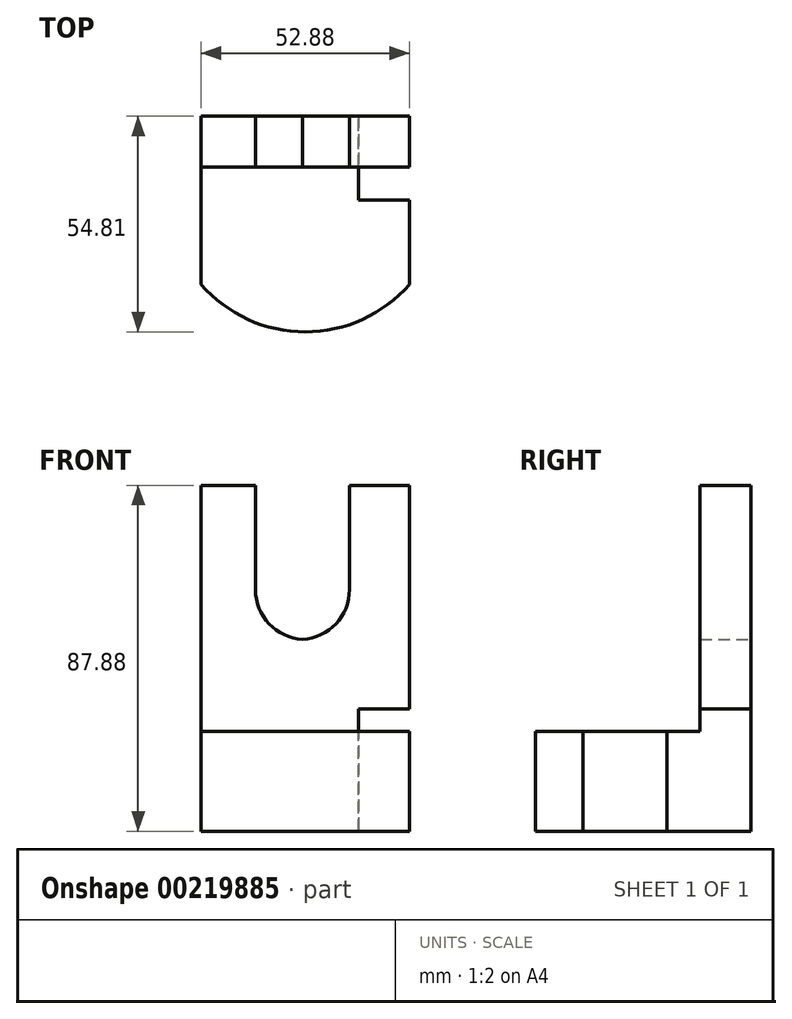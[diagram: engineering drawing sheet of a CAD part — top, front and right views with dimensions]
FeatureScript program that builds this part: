
annotation { "Feature Type Name" : "Feature", "Feature Type Description" : "" }
export const myFeature = defineFeature(function(context is Context, id is Id, definition is map)
    precondition{}
    {
        {
            var Q0;
            Q0=qCreatedBy(makeId("Top.planeOp"),FACE);
            var sketch = newSketch(context, id + "F0", { "sketchPlane" : qUnion([Q0])});
            skLineSegment(sketch, "E0", {"start": v(-27.7, 17.9) * mm, "end": v(25.17, 17.9) * mm});
            skLineSegment(sketch, "E1", {"start": v(25.17, 17.9) * mm, "end": v(25.17, -11.9) * mm});
            skLineSegment(sketch, "E2", {"start": v(-27.7, 17.9) * mm, "end": v(-27.7, -11.9) * mm});
            skArc(sketch, "E3", {"start": v(-27.7, -11.9) * mm, "mid": v(-1.27, -23.98) * mm, "end": v(25.17, -11.9) * mm});
            skSolve(sketch);
        }
        {
            var Q0;
            Q0 = qSketchRegion(id + "F0", true);
            extrude(context, id + "F1", {"entities" : qUnion([Q0]), "depth" : 25.4 * mm});
        }
        {
            var Q0;
            Q0=makeQuery(id+"F1.opExtrude","CAP_FACE",FACE,{"disambiguationData":[OSD([sQuery(id+"F0.wireOp",EDGE,"E0"),sQuery(id+"F0.wireOp",EDGE,"E1"),sQuery(id+"F0.wireOp",EDGE,"E2"),sQuery(id+"F0.wireOp",EDGE,"E3")])],"isStart":true});
            var sketch = newSketch(context, id + "F2", { "sketchPlane" : qUnion([Q0])});
            skLineSegment(sketch, "E4", {"start": v(-27.7, -17.9) * mm, "end": v(25.17, -17.9) * mm});
            skLineSegment(sketch, "E5", {"start": v(25.17, -17.9) * mm, "end": v(25.17, -30.83) * mm});
            skLineSegment(sketch, "E6", {"start": v(25.17, -30.83) * mm, "end": v(-27.7, -30.83) * mm});
            skLineSegment(sketch, "E7", {"start": v(-27.7, -30.83) * mm, "end": v(-27.7, -17.9) * mm});
            skSolve(sketch);
        }
        {
            var Q0;
            Q0 = qSketchRegion(id + "F2", true);
            extrude(context, id + "F3", {"entities" : qUnion([Q0]), "operationType" : NewBodyOperationType.ADD, "oppositeDirection" : true, "depth" : 87.88 * mm});
        }
        {
            var Q0;
            Q0=makeQuery(id+"F3.opExtrude","SWEPT_FACE",FACE,{"disambiguationData":[OSD([sQuery(id+"F2.wireOp",EDGE,"E4")])]});
            var sketch = newSketch(context, id + "F4", { "sketchPlane" : qUnion([Q0])});
            skLineSegment(sketch, "E8.bottom", {"start": v(-13.92, 87.88) * mm, "end": v(9.94, 87.88) * mm});
            skLineSegment(sketch, "E8.top", {"start": v(-13.92, 48.73) * mm, "end": v(9.94, 48.73) * mm});
            skLineSegment(sketch, "E8.left", {"start": v(-13.92, 87.88) * mm, "end": v(-13.92, 48.73) * mm});
            skLineSegment(sketch, "E8.right", {"start": v(9.94, 87.88) * mm, "end": v(9.94, 48.73) * mm});
            skSolve(sketch);
        }
        {
            var Q0;
            Q0 = qSketchRegion(id + "F4", true);
            extrude(context, id + "F5", {"entities" : qUnion([Q0]), "operationType" : NewBodyOperationType.REMOVE, "oppositeDirection" : true, "depth" : 25.4 * mm});
        }
        {
            var Q0;
            Q0=makeQuery(id+"F5.boolean.opBoolean","COPY",EDGE,{"derivedFrom":makeQuery(id+"F5.opExtrude","SWEPT_EDGE",EDGE,{"disambiguationData":[OSD([sQuery(id+"F4.wireOp",EDGE,"E8.top"),sQuery(id+"F4.wireOp",EDGE,"E8.left")])]})});
            var Q1;
            Q1=makeQuery(id+"F5.boolean.opBoolean","COPY",EDGE,{"derivedFrom":makeQuery(id+"F5.opExtrude","SWEPT_EDGE",EDGE,{"disambiguationData":[OSD([sQuery(id+"F4.wireOp",EDGE,"E8.top"),sQuery(id+"F4.wireOp",EDGE,"E8.right")])]})});
            fillet(context, id + "F6", {"entities" : qUnion([Q0, Q1]), "radius" : 12.7 * mm, "tangentPropagation" : true, "allowEdgeOverflow" : false});
        }
        {
            var Q0;
            Q0=makeQuery(id+"F3.boolean.opBoolean","MERGE",FACE,{"derivedFrom":[makeQuery(id+"F1.opExtrude","SWEPT_FACE",FACE,{"disambiguationData":[OSD([sQuery(id+"F0.wireOp",EDGE,"E1")])]}),makeQuery(id+"F3.opExtrude","SWEPT_FACE",FACE,{"disambiguationData":[OSD([sQuery(id+"F2.wireOp",EDGE,"E5")])]})]});
            var sketch = newSketch(context, id + "F7", { "sketchPlane" : qUnion([Q0])});
            skLineSegment(sketch, "E9", {"start": v(30.83, 31.08) * mm, "end": v(30.83, 0) * mm});
            skLineSegment(sketch, "E10", {"start": v(30.83, 0) * mm, "end": v(9.47, 0) * mm});
            skLineSegment(sketch, "E11", {"start": v(9.47, 0) * mm, "end": v(9.47, 25.4) * mm});
            skLineSegment(sketch, "E12", {"start": v(9.47, 25.4) * mm, "end": v(17.9, 25.4) * mm});
            skLineSegment(sketch, "E13", {"start": v(17.9, 25.4) * mm, "end": v(17.9, 31.08) * mm});
            skLineSegment(sketch, "E14", {"start": v(17.9, 31.08) * mm, "end": v(30.83, 31.08) * mm});
            skSolve(sketch);
        }
        {
            var Q0;
            Q0 = qSketchRegion(id + "F7", true);
            extrude(context, id + "F8", {"entities" : qUnion([Q0]), "operationType" : NewBodyOperationType.REMOVE, "oppositeDirection" : true, "depth" : 12.95 * mm});
        }
    });
